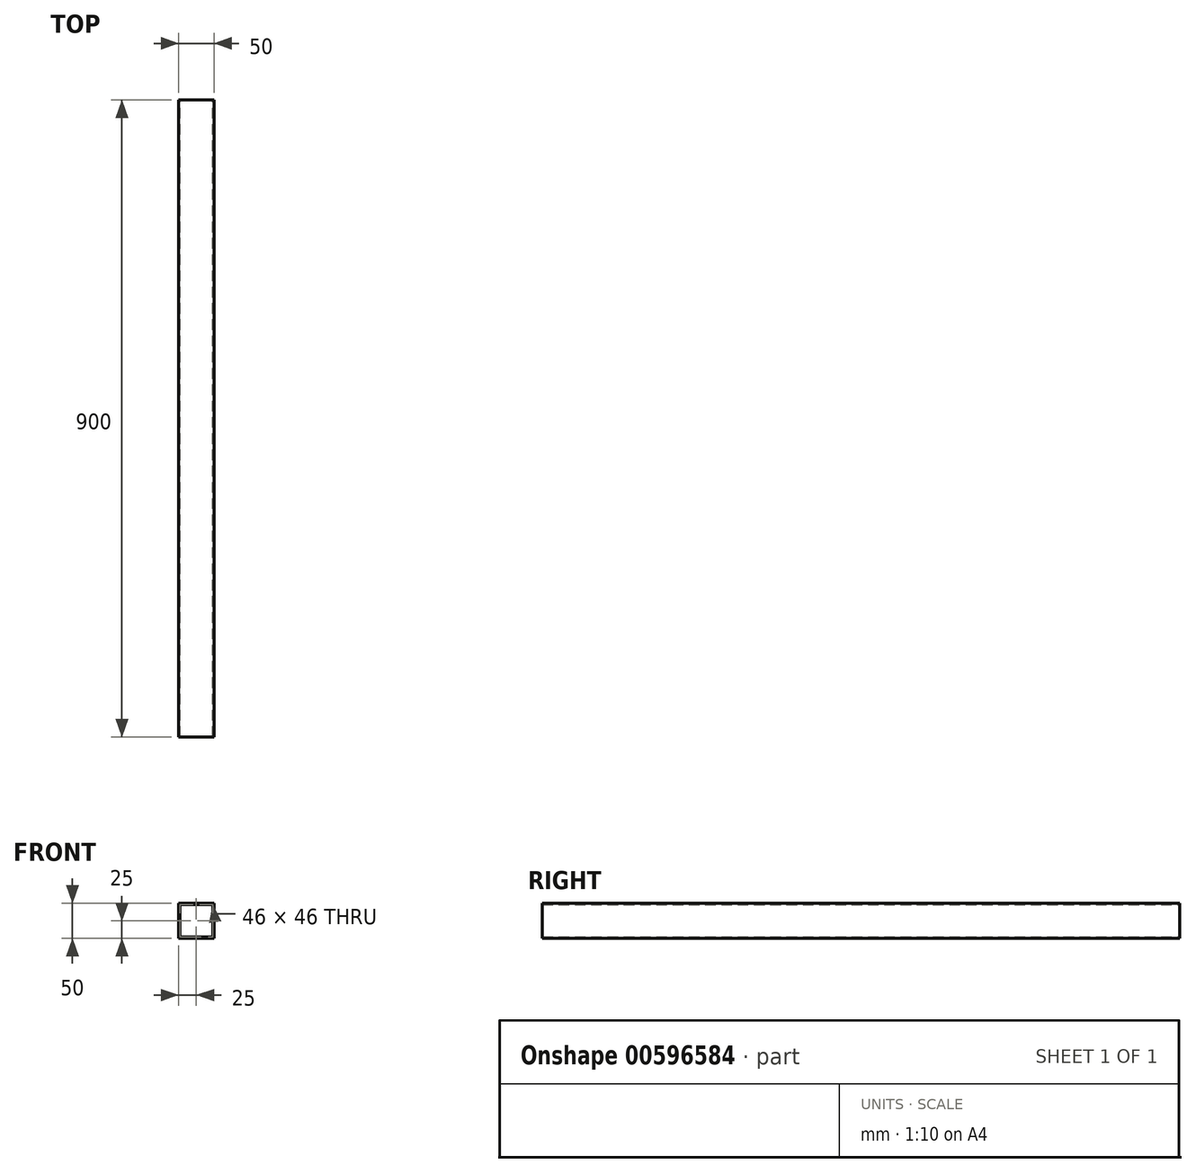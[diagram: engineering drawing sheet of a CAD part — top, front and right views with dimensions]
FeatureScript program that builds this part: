
annotation { "Feature Type Name" : "Feature", "Feature Type Description" : "" }
export const myFeature = defineFeature(function(context is Context, id is Id, definition is map)
    precondition{}
    {
        {
            var Q0;
            Q0=qCreatedBy(makeId("Front.planeOp"),FACE);
            var sketch = newSketch(context, id + "F0", { "sketchPlane" : qUnion([Q0])});
            skLineSegment(sketch, "E0.bottom", {"start": v(0, 0) * mm, "end": v(50, 0) * mm});
            skLineSegment(sketch, "E0.top", {"start": v(0, 50) * mm, "end": v(50, 50) * mm});
            skLineSegment(sketch, "E0.left", {"start": v(0, 0) * mm, "end": v(0, 50) * mm});
            skLineSegment(sketch, "E0.right", {"start": v(50, 0) * mm, "end": v(50, 50) * mm});
            skLineSegment(sketch, "E1.0", {"start": v(2, 48) * mm, "end": v(48, 48) * mm});
            skLineSegment(sketch, "E2.0", {"start": v(2, 2) * mm, "end": v(2, 48) * mm});
            skLineSegment(sketch, "E3.0", {"start": v(2, 2) * mm, "end": v(48, 2) * mm});
            skLineSegment(sketch, "E4.0", {"start": v(48, 2) * mm, "end": v(48, 48) * mm});
            skSolve(sketch);
        }
        {
            var Q0;
            Q0=makeQuery(id+"F0.imprint","IMPRINT",FACE,{"disambiguationData":[TD([[makeQuery(id+"F0.imprint","IMPRINT",EDGE,{"derivedFrom":sQuery(id+"F0.wireOp",EDGE,"E0.bottom")}),1.0]])]});
            extrude(context, id + "F1", {"entities" : qUnion([Q0]), "depth" : 900 * mm, "offsetDistance" : 25 * mm});
        }
    });
